# Revit family: Hydrant_Wall_Narrow-Zurn-Z1325-Encased Vari-Temp
name_source: partatom
category: Plumbing Fixtures
units: mm (PartAtom-declared; Revit-internal decimal feet)

## family parameters
Cut with Voids When Loaded = No
Host = Face
Maintain Annotation Orientation = No
OmniClass Number = 23.65.70.14.11.11
OmniClass Title = Security Drinking Fountains/Coolers
Part Type = Normal
Room Calculation Point = No
Round Connector Dimension = Use Radius
Shared = No

## types (16) — shared parameters
3/4 Inch Hose Connection Radius = 0.375 "
Assembly Code = D2020100
Box and Cover = Bronze - Zurn - Polished Nickel
CW Connection = Yes
CWFU = 1
Default Elevation = 25 "
Description = Wall Hydrant, Encased Vari-Temp, Non-Freeze
HW Connection = Yes
HWFU = 1
Height = 10.5 "
Housing = Bronze - Zurn - Polished
Manufacturer = Zurn Water, LLC
Manufacturer Brand = Zurn
Model = Z1325
Modified Date = 10/10/2025
Piping = Copper - Zurn - ASTM B88 Type L - Seamless Water Tube
Product Documentation Link = https://files.zurn.com
Product Installation Sheet URL = https://files.zurn.com
Product Page URL = https://www.bimobject.com
Product data url = https://www.zurn.com
URL = www.zurn.com
Vacuum Breaker = Brass - Zurn - Polished
Vent Connection = No
Waste Connection = No
Width = 10.5 "
zero-valued in all types: WFU

## per-type parameters (varying)
| type | Approx.Wt. Lbs. | Female And Male Inlet Radius | Female and Male Inlet Connector | Type Comments | Wall Thickness |
| Z1325 - 6" Wall Hydrant w/ 3/4" Female Inlet | 27 " | 0.525 " | 0.375 " | Z1325 - 6 Inch Wall Hydrant with 3/4 Inch Female Inlet | 6 " |
| Z1325 - 6" Wall Hydrant w/ 1" Male Inlet | 27 " | 0.658 " | 0.5 " | Z1325 - 6 Inch Wall Hydrant with 1 Inch Male Inlet | 6 " |
| Z1325 - 8" Wall Hydrant w/ 3/4" Female Inlet | 27 " | 0.525 " | 0.375 " | Z1325 - 8 Inch Wall Hydrant with 3/4 Inch Female Inlet | 8 " |
| Z1325 - 8" Wall Hydrant w/ 1" Male Inlet | 27 " | 0.658 " | 0.5 " | Z1325 - 8 Inch Wall Hydrant with 1 Inch Male Inlet | 8 " |
| Z1325 - 10" Wall Hydrant w/ 3/4" Female Inlet | 31 " | 0.525 " | 0.375 " | Z1325 - 10 Inch Wall Hydrant with 3/4 Inch Female Inlet | 10 " |
| Z1325 - 10" Wall Hydrant w/ 1" Male Inlet | 31 " | 0.658 " | 0.5 " | Z1325 - 10 Inch Wall Hydrant with 1 Inch Male Inlet | 10 " |
| Z1325 - 12" Wall Hydrant w/ 3/4" Female Inlet | 31 " | 0.525 " | 0.375 " | Z1325 - 12 Inch Wall Hydrant with 3/4 Inch Female Inlet | 12 " |
| Z1325 - 12" Wall Hydrant w/ 1" Male Inlet | 31 " | 0.658 " | 0.5 " | Z1325 - 12 Inch Wall Hydrant with 1 Inch Male Inlet | 12 " |
| Z1325 - 14" Wall Hydrant w/ 3/4" Female Inlet | 31 " | 0.525 " | 0.375 " | Z1325 - 14 Inch Wall Hydrant with 3/4 Inch Female Inlet | 14 " |
| Z1325 - 14" Wall Hydrant w/ 1" Male Inlet | 31 " | 0.658 " | 0.5 " | Z1325 - 14 Inch Wall Hydrant with 1 Inch Male Inlet | 14 " |
| Z1325 - 16" Wall Hydrant w/ 3/4" Female Inlet | 35 " | 0.525 " | 0.375 " | Z1325 - 16 Inch Wall Hydrant with 3/4 Inch Female Inlet | 16 " |
| Z1325 - 16" Wall Hydrant w/ 1" Male Inlet | 35 " | 0.658 " | 0.5 " | Z1325 - 16 Inch Wall Hydrant with 1 Inch Male Inlet | 16 " |
| Z1325 - 18" Wall Hydrant w/ 3/4" Female Inlet | 35 " | 0.525 " | 0.375 " | Z1325 - 18 Inch Wall Hydrant with 3/4 Inch Female Inlet | 18 " |
| Z1325 - 18" Wall Hydrant w/ 1" Male Inlet | 35 " | 0.658 " | 0.5 " | Z1325 - 18 Inch Wall Hydrant with 1 Inch Male Inlet | 18 " |
| Z1325 - 24" Wall Hydrant w/ 3/4" Female Inlet | 39 " | 0.525 " | 0.375 " | Z1325 - 24 Inch Wall Hydrant with 3/4 Inch Female Inlet | 24 " |
| Z1325 - 24" Wall Hydrant w/ 1" Male Inlet | 39 " | 0.658 " | 0.5 " | Z1325 - 24 Inch Wall Hydrant with 1 Inch Male Inlet | 24 " |

## geometry (parser evidence)
native form markers: Blend x10, Sweep x2
no freeform markers — native parametric forms only
